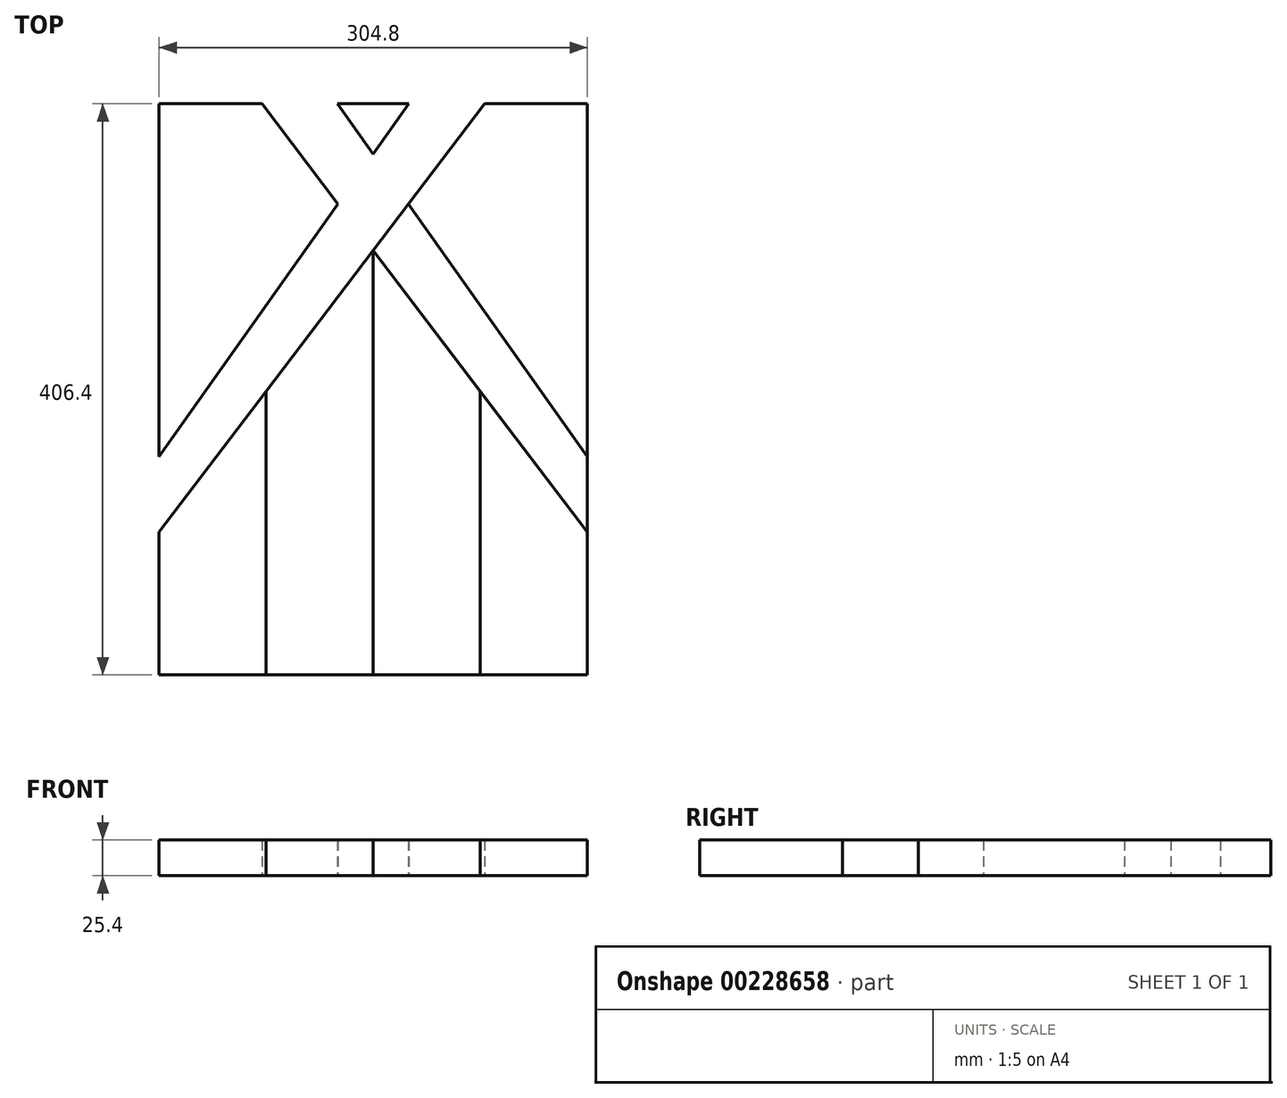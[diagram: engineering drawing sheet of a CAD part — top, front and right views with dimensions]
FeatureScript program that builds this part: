
annotation { "Feature Type Name" : "Feature", "Feature Type Description" : "" }
export const myFeature = defineFeature(function(context is Context, id is Id, definition is map)
    precondition{}
    {
        {
            var Q0;
            Q0=qCreatedBy(makeId("Top.planeOp"),FACE);
            var sketch = newSketch(context, id + "F0", { "sketchPlane" : qUnion([Q0])});
            skLineSegment(sketch, "E0.bottom", {"start": v(152.4, -203.2) * mm, "end": v(-152.4, -203.2) * mm});
            skLineSegment(sketch, "E0.top", {"start": v(152.4, 203.2) * mm, "end": v(-152.4, 203.2) * mm});
            skLineSegment(sketch, "E0.left", {"start": v(152.4, -203.2) * mm, "end": v(152.4, 203.2) * mm});
            skLineSegment(sketch, "E0.right", {"start": v(-152.4, -203.2) * mm, "end": v(-152.4, 203.2) * mm});
            skPoint(sketch, "E0.middle", {"position": v(0, 0) * mm});
            skLineSegment(sketch, "E1", {"start": v(152.4, -203.2) * mm, "end": v(152.4, -101.6) * mm});
            skLineSegment(sketch, "E2", {"start": v(-152.4, 203.2) * mm, "end": v(-79.27, 203.2) * mm});
            skLineSegment(sketch, "E3", {"start": v(-79.27, 203.2) * mm, "end": v(152.4, -101.6) * mm});
            skLineSegment(sketch, "E4", {"start": v(152.4, -101.6) * mm, "end": v(152.4, -47.73) * mm});
            skLineSegment(sketch, "E5", {"start": v(-152.4, 203.2) * mm, "end": v(-25.4, 203.2) * mm});
            skLineSegment(sketch, "E6", {"start": v(-25.4, 203.2) * mm, "end": v(152.4, -47.73) * mm});
            skLineSegment(sketch, "E7", {"start": v(152.4, 203.2) * mm, "end": v(25.4, 203.2) * mm});
            skLineSegment(sketch, "E8", {"start": v(152.4, 203.2) * mm, "end": v(79.27, 203.2) * mm});
            skLineSegment(sketch, "E9", {"start": v(79.27, 203.2) * mm, "end": v(-152.4, -101.6) * mm});
            skLineSegment(sketch, "E10", {"start": v(25.4, 203.2) * mm, "end": v(-152.4, -47.73) * mm});
            skLineSegment(sketch, "E11", {"start": v(-152.4, -203.2) * mm, "end": v(0, -203.2) * mm});
            skLineSegment(sketch, "E12", {"start": v(0, -203.2) * mm, "end": v(152.4, -203.2) * mm});
            skLineSegment(sketch, "E13", {"start": v(76.2, -203.2) * mm, "end": v(76.2, -1.35) * mm});
            skLineSegment(sketch, "E14", {"start": v(-76.2, -203.2) * mm, "end": v(-76.2, -1.35) * mm});
            skLineSegment(sketch, "E15", {"start": v(0, -203.2) * mm, "end": v(0, 98.9) * mm});
            skLineSegment(sketch, "E16", {"start": v(-79.27, 203.2) * mm, "end": v(-152.4, 203.2) * mm});
            skLineSegment(sketch, "E17", {"start": v(0, 98.9) * mm, "end": v(152.4, -101.6) * mm});
            skLineSegment(sketch, "E18", {"start": v(-79.27, 203.2) * mm, "end": v(-25.1, 131.93) * mm});
            skPoint(sketch, "E19", {"position": v(0, 167.35) * mm});
            skLineSegment(sketch, "E20", {"start": v(-152.4, -47.73) * mm, "end": v(-152.4, 203.2) * mm});
            skLineSegment(sketch, "E21", {"start": v(152.4, -47.73) * mm, "end": v(25.1, 131.93) * mm});
            skSolve(sketch);
        }
        {
            var Q0;
            {var subQ5=sQuery(id+"F0.wireOp",EDGE,"E14");Q0=makeQuery(id+"F0.imprint","IMPRINT",FACE,{"disambiguationData":[TD([[makeQuery(id+"F0.imprint","IMPRINT",EDGE,{"derivedFrom":subQ5}),1.0]])]});}
            var Q1;
            {var subQ0=sQuery(id+"F0.wireOp",EDGE,"E5");var subQ1=sQuery(id+"F0.wireOp",EDGE,"E0.right");var subQ2=makeQuery(id+"F0.imprint","INTERSECT",VERTEX,{"derivedFrom":[subQ1,subQ0]});Q1=makeQuery(id+"F0.imprint","IMPRINT",FACE,{"disambiguationData":[TD([[makeQuery(id+"F0.imprint","IMPRINT",EDGE,{"disambiguationData":[TD([[subQ2,1.0]])],"derivedFrom":subQ1}),-1.0]])]});}
            var Q2;
            {var subQ0=sQuery(id+"F0.wireOp",EDGE,"E0.top");Q2=makeQuery(id+"F0.imprint","IMPRINT",FACE,{"disambiguationData":[TD([[makeQuery(id+"F0.imprint","IMPRINT",EDGE,{"derivedFrom":subQ0}),1.0]])]});}
            var Q3;
            {var subQ0=sQuery(id+"F0.wireOp",EDGE,"E0.left");Q3=makeQuery(id+"F0.imprint","IMPRINT",FACE,{"disambiguationData":[TD([[makeQuery(id+"F0.imprint","IMPRINT",EDGE,{"derivedFrom":subQ0}),1.0]])]});}
            var Q4;
            {var subQ0=sQuery(id+"F0.wireOp",EDGE,"E1");Q4=makeQuery(id+"F0.imprint","IMPRINT",FACE,{"disambiguationData":[TD([[makeQuery(id+"F0.imprint","IMPRINT",EDGE,{"derivedFrom":subQ0}),1.0]])]});}
            extrude(context, id + "F1", {"entities" : qUnion([Q0, Q1, Q2, Q3, Q4]), "depth" : 25.4 * mm, "offsetDistance" : 25.4 * mm});
        }
        {
            var Q0;
            Q0=makeQuery(id+"F1.opExtrude","SWEPT_BODY",BODY,{"disambiguationData":[OSD([sQuery(id+"F0.wireOp",EDGE,"E0.right"),sQuery(id+"F0.wireOp",EDGE,"E9"),sQuery(id+"F0.wireOp",EDGE,"E11"),sQuery(id+"F0.wireOp",EDGE,"E14")])]});
            var Q1;
            Q1=makeQuery(id+"F1.opExtrude","SWEPT_BODY",BODY,{"disambiguationData":[OSD([sQuery(id+"F0.wireOp",EDGE,"E1"),sQuery(id+"F0.wireOp",EDGE,"E12"),sQuery(id+"F0.wireOp",EDGE,"E13"),sQuery(id+"F0.wireOp",EDGE,"E17")])]});
            var Q2;
            Q2=makeQuery(id+"F1.opExtrude","SWEPT_BODY",BODY,{"disambiguationData":[OSD([sQuery(id+"F0.wireOp",EDGE,"E0.left"),sQuery(id+"F0.wireOp",EDGE,"E8"),sQuery(id+"F0.wireOp",EDGE,"E9"),sQuery(id+"F0.wireOp",EDGE,"E21")])]});
            var Q3;
            Q3=makeQuery(id+"F1.opExtrude","SWEPT_BODY",BODY,{"disambiguationData":[OSD([sQuery(id+"F0.wireOp",EDGE,"E0.top"),sQuery(id+"F0.wireOp",EDGE,"E6"),sQuery(id+"F0.wireOp",EDGE,"E10")])]});
            deleteBodies(context, id + "F2", {"entities" : qUnion([Q0, Q1, Q2, Q3])});
        }
        {
            var Q0;
            {var subQ5=sQuery(id+"F0.wireOp",EDGE,"E14");Q0=makeQuery(id+"F0.imprint","IMPRINT",FACE,{"disambiguationData":[TD([[makeQuery(id+"F0.imprint","IMPRINT",EDGE,{"derivedFrom":subQ5}),1.0]])]});}
            var Q1;
            {var subQ0=sQuery(id+"F0.wireOp",EDGE,"E1");Q1=makeQuery(id+"F0.imprint","IMPRINT",FACE,{"disambiguationData":[TD([[makeQuery(id+"F0.imprint","IMPRINT",EDGE,{"derivedFrom":subQ0}),1.0]])]});}
            var Q2;
            Q2=makeQuery(id+"F0.imprint","IMPRINT",FACE,{"disambiguationData":[TD([[makeQuery(id+"F0.imprint","IMPRINT",EDGE,{"derivedFrom":sQuery(id+"F0.wireOp",EDGE,"E0.left")}),1.0]])]});
            var Q3;
            Q3=makeQuery(id+"F0.imprint","IMPRINT",FACE,{"disambiguationData":[TD([[makeQuery(id+"F0.imprint","IMPRINT",EDGE,{"derivedFrom":sQuery(id+"F0.wireOp",EDGE,"E16")}),1.0]])]});
            var Q4;
            {var subQ0=sQuery(id+"F0.wireOp",EDGE,"E0.top");Q4=makeQuery(id+"F0.imprint","IMPRINT",FACE,{"disambiguationData":[TD([[makeQuery(id+"F0.imprint","IMPRINT",EDGE,{"derivedFrom":subQ0}),1.0]])]});}
            extrude(context, id + "F3", {"entities" : qUnion([Q0, Q1, Q2, Q3, Q4]), "depth" : 25.4 * mm, "offsetDistance" : 25.4 * mm});
        }
        {
            var Q0;
            {var subQ0=sQuery(id+"F0.wireOp",EDGE,"E3");Q0=makeQuery(id+"F0.imprint","IMPRINT",FACE,{"disambiguationData":[TD([[makeQuery(id+"F0.imprint","IMPRINT",EDGE,{"derivedFrom":subQ0}),1.0]])]});}
            extrude(context, id + "F4", {"entities" : qUnion([Q0]), "depth" : 25.4 * mm, "offsetDistance" : 25.4 * mm});
        }
        {
            var Q0;
            {var subQ1=sQuery(id+"F0.wireOp",EDGE,"E3");Q0=makeQuery(id+"F0.imprint","IMPRINT",FACE,{"disambiguationData":[TD([[makeQuery(id+"F0.imprint","IMPRINT",EDGE,{"derivedFrom":subQ1}),-1.0]])]});}
            var Q1;
            {var subQ0=sQuery(id+"F0.wireOp",EDGE,"E5");Q1=makeQuery(id+"F0.imprint","IMPRINT",FACE,{"disambiguationData":[TD([[makeQuery(id+"F0.imprint","IMPRINT",EDGE,{"derivedFrom":subQ0}),-1.0]])]});}
            var Q2;
            {var subQ5=sQuery(id+"F0.wireOp",EDGE,"E7");Q2=makeQuery(id+"F0.imprint","IMPRINT",FACE,{"disambiguationData":[TD([[makeQuery(id+"F0.imprint","IMPRINT",EDGE,{"derivedFrom":subQ5}),1.0]])]});}
            var Q3;
            {var subQ4=sQuery(id+"F0.wireOp",EDGE,"E4");Q3=makeQuery(id+"F0.imprint","IMPRINT",FACE,{"disambiguationData":[TD([[makeQuery(id+"F0.imprint","IMPRINT",EDGE,{"derivedFrom":subQ4}),1.0]])]});}
            extrude(context, id + "F5", {"entities" : qUnion([Q0, Q1, Q2, Q3]), "depth" : 25.4 * mm, "offsetDistance" : 25.4 * mm});
        }
        {
            var Q0;
            {var subQ2=sQuery(id+"F0.wireOp",EDGE,"E13");Q0=makeQuery(id+"F0.imprint","IMPRINT",FACE,{"disambiguationData":[TD([[makeQuery(id+"F0.imprint","IMPRINT",EDGE,{"derivedFrom":subQ2}),1.0]])]});}
            var Q1;
            {var subQ2=sQuery(id+"F0.wireOp",EDGE,"E14");Q1=makeQuery(id+"F0.imprint","IMPRINT",FACE,{"disambiguationData":[TD([[makeQuery(id+"F0.imprint","IMPRINT",EDGE,{"derivedFrom":subQ2}),-1.0]])]});}
            extrude(context, id + "F6", {"entities" : qUnion([Q0, Q1]), "depth" : 25.4 * mm, "offsetDistance" : 25.4 * mm});
        }
    });
